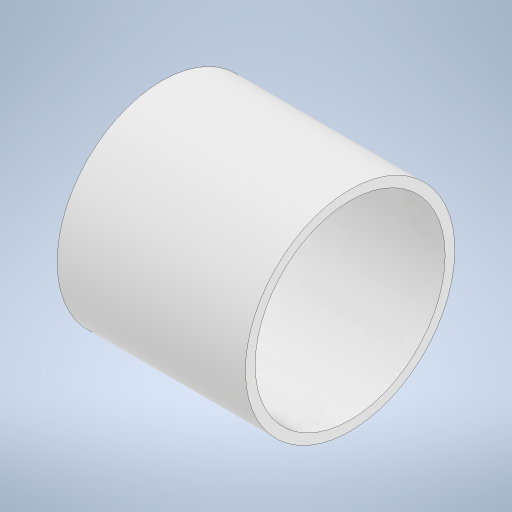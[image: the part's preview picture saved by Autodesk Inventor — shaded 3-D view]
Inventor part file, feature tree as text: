
AUTODESK INVENTOR PART (.ipt)
format: ipt  version: 2023 (Build 270158030, 158C)  size: 218,624 bytes
history: native  units: in
note: dims shown in document units (in); Inventor stores cm internally (conversion verified against a paired STEP export)
features: extrude x1, sketch x1
ambient origin geometry x8: Origin, YZ Plane, XZ Plane, XY Plane, X Axis, Y Axis, Z Axis, Center Point
bodies: Solid1 (feature_tree)
feature tree (2):
  extrude  "Extrusion1"  Depth=5.0in
  sketch  "Sketch1"  dims[d0=5.047in d1=0.258in d2=5.0in d3=0.0in d4=0.5in d5=0.0344in d6=0.5in d7=0.0344in]
